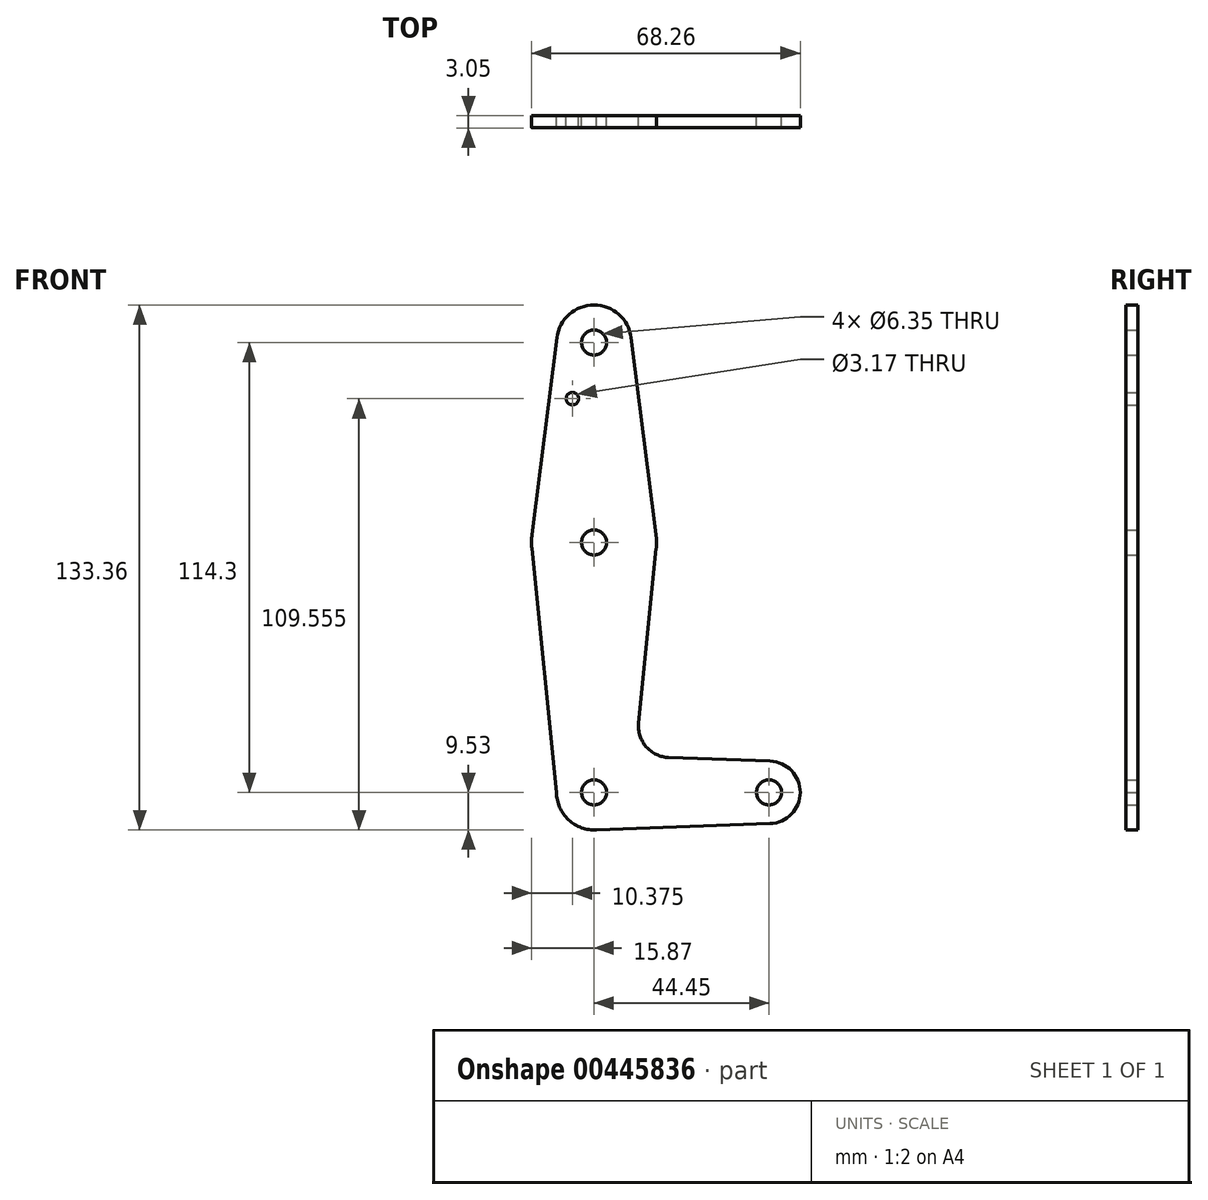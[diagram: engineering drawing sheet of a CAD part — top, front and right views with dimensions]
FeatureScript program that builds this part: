
annotation { "Feature Type Name" : "Feature", "Feature Type Description" : "" }
export const myFeature = defineFeature(function(context is Context, id is Id, definition is map)
    precondition{}
    {
        {
            var Q0;
            Q0=qCreatedBy(makeId("Front.planeOp"),FACE);
            var sketch = newSketch(context, id + "F0", { "sketchPlane" : qUnion([Q0])});
            skLineSegment(sketch, "E0", {"start": v(0, 0) * mm, "end": v(0, 114.3) * mm, "construction": true});
            skLineSegment(sketch, "E1", {"start": v(0, 0) * mm, "end": v(44.45, 0) * mm, "construction": true});
            skCircle(sketch, "E2", {"center": v(0, 114.3) * mm, "radius": 9.53 * mm});
            skCircle(sketch, "E3", {"center": v(0, 0) * mm, "radius": 9.53 * mm});
            skCircle(sketch, "E4", {"center": v(44.45, 0) * mm, "radius": 7.94 * mm});
            skCircle(sketch, "E5", {"center": v(0, 63.5) * mm, "radius": 15.88 * mm});
            skLineSegment(sketch, "E6", {"start": v(15.75, 65.48) * mm, "end": v(9.45, 115.5) * mm});
            skLineSegment(sketch, "E7", {"start": v(-15.75, 65.48) * mm, "end": v(-9.45, 115.5) * mm});
            skCircle(sketch, "E8", {"center": v(0, 114.3) * mm, "radius": 3.18 * mm});
            skCircle(sketch, "E9", {"center": v(0, 63.5) * mm, "radius": 3.18 * mm});
            skCircle(sketch, "E10", {"center": v(0, 0) * mm, "radius": 3.18 * mm});
            skCircle(sketch, "E11", {"center": v(44.45, 0) * mm, "radius": 3.18 * mm});
            skCircle(sketch, "E12", {"center": v(-5.5, 100.03) * mm, "radius": 1.59 * mm});
            skLineSegment(sketch, "E13", {"start": v(15.8, 61.91) * mm, "end": v(11.34, 17.6) * mm});
            skLineSegment(sketch, "E14", {"start": v(44.73, 7.93) * mm, "end": v(18.97, 8.85) * mm});
            skLineSegment(sketch, "E15", {"start": v(0, -9.53) * mm, "end": v(44.73, -7.93) * mm});
            skPoint(sketch, "E16.newPointB", {"position": v(0, 9.53) * mm});
            skArc(sketch, "E16.filletArc", {"start": v(11.34, 17.6) * mm, "mid": v(13.26, 11.57) * mm, "end": v(18.97, 8.85) * mm});
            skLineSegment(sketch, "E17", {"start": v(-9.53, 0) * mm, "end": v(-15.8, 61.9) * mm});
            skSolve(sketch);
        }
        {
            var Q0;
            Q0 = qSketchRegion(id + "F0", true);
            extrude(context, id + "F1", {"entities" : qUnion([Q0]), "depth" : 3.05 * mm});
        }
    });
